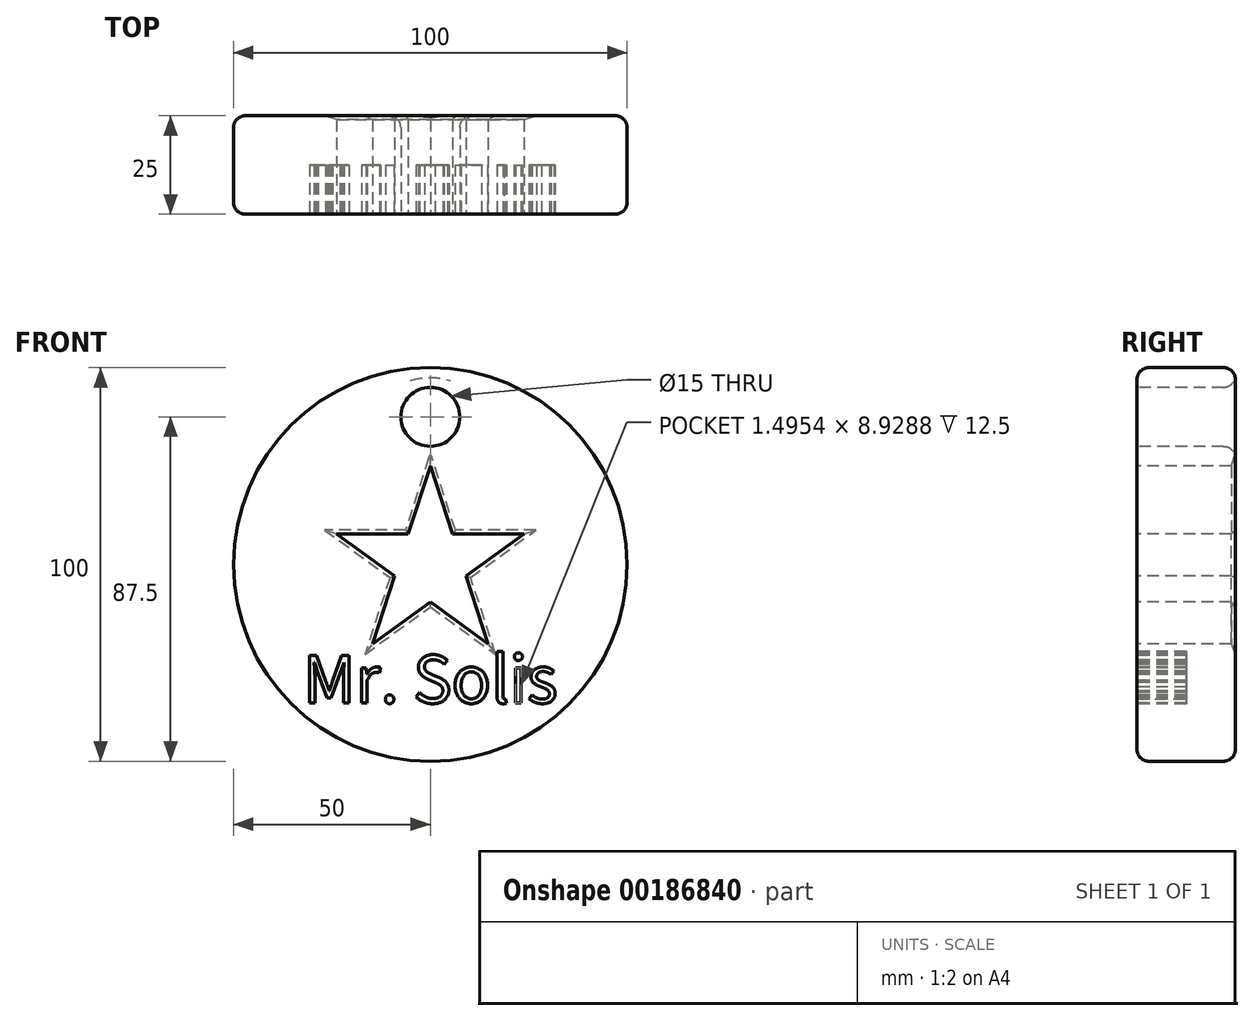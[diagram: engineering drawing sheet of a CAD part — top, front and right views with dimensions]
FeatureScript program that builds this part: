
annotation { "Feature Type Name" : "Feature", "Feature Type Description" : "" }
export const myFeature = defineFeature(function(context is Context, id is Id, definition is map)
    precondition{}
    {
        {
            var Q0;
            Q0=qCreatedBy(makeId("Front.planeOp"),FACE);
            var sketch = newSketch(context, id + "F0", { "sketchPlane" : qUnion([Q0])});
            skCircle(sketch, "E0", {"center": v(0, 0) * mm, "radius": 50 * mm});
            skSolve(sketch);
        }
        {
            var Q0;
            Q0 = qSketchRegion(id + "F0", true);
            extrude(context, id + "F1", {"entities" : qUnion([Q0]), "depth" : 12.5 * mm, "hasSecondDirection" : true, "secondDirectionOppositeDirection" : true, "secondDirectionDepth" : 12.5 * mm});
        }
        {
            var Q0;
            Q0=makeQuery(id+"F1.opExtrude","CAP_FACE",FACE,{"disambiguationData":[OSD([sQuery(id+"F0.wireOp",EDGE,"E0")])],"isStart":false});
            var sketch = newSketch(context, id + "F2", { "sketchPlane" : qUnion([Q0])});
            skCircle(sketch, "E1", {"center": v(0, 37.5) * mm, "radius": 7.5 * mm});
            skSolve(sketch);
        }
        {
            var Q0;
            Q0 = qSketchRegion(id + "F2", true);
            var Q1;
            Q1=makeQuery(id+"F2.imprint","IMPRINT",FACE,{"disambiguationData":[TD([[makeQuery(id+"F2.imprint","IMPRINT",EDGE,{"derivedFrom":sQuery(id+"F2.wireOp",EDGE,"E1")}),1.0]])]});
            extrude(context, id + "F3", {"entities" : qUnion([Q0, Q1]), "operationType" : NewBodyOperationType.REMOVE, "oppositeDirection" : true, "depth" : 26 * mm});
        }
        {
            var Q0;
            Q0=makeQuery(id+"F1.opExtrude","CAP_FACE",FACE,{"disambiguationData":[OSD([sQuery(id+"F0.wireOp",EDGE,"E0")])],"isStart":false});
            var sketch = newSketch(context, id + "F4", { "sketchPlane" : qUnion([Q0])});
            skArc(sketch, "E2.cCircle", {"start": v(1.57, 20.16) * mm, "mid": v(0, 20.23) * mm, "end": v(-1.57, 20.16) * mm, "construction": true});
            skLineSegment(sketch, "E2.0", {"start": v(23.78, 7.73) * mm, "end": v(14.7, -20.23) * mm});
            skLineSegment(sketch, "E2.1", {"start": v(14.7, -20.23) * mm, "end": v(-14.7, -20.23) * mm});
            skLineSegment(sketch, "E2.2", {"start": v(-14.7, -20.23) * mm, "end": v(-23.78, 7.73) * mm});
            skLineSegment(sketch, "E2.3", {"start": v(-23.78, 7.73) * mm, "end": v(0, 25) * mm});
            skLineSegment(sketch, "E2.4", {"start": v(0, 25) * mm, "end": v(23.78, 7.73) * mm});
            skPoint(sketch, "E2.0.midPoint", {"position": v(19.24, -6.25) * mm});
            skLineSegment(sketch, "E3", {"start": v(0, 25) * mm, "end": v(-5.61, 7.73) * mm});
            skLineSegment(sketch, "E4", {"start": v(-23.78, 7.73) * mm, "end": v(-5.61, 7.73) * mm});
            skLineSegment(sketch, "E5", {"start": v(0, 25) * mm, "end": v(5.61, 7.73) * mm});
            skLineSegment(sketch, "E6", {"start": v(-14.7, -20.23) * mm, "end": v(0, -9.55) * mm});
            skLineSegment(sketch, "E7", {"start": v(-23.78, 7.73) * mm, "end": v(-9.08, -2.95) * mm});
            skLineSegment(sketch, "E8.trimOffspring", {"start": v(5.61, 7.73) * mm, "end": v(23.78, 7.73) * mm});
            skLineSegment(sketch, "E9.trimOffspring", {"start": v(-9.08, -2.95) * mm, "end": v(-14.7, -20.23) * mm});
            skLineSegment(sketch, "E10.trimOffspring", {"start": v(9.08, -2.95) * mm, "end": v(14.7, -20.23) * mm});
            skLineSegment(sketch, "E11.trimOffspring", {"start": v(9.08, -2.95) * mm, "end": v(23.78, 7.73) * mm});
            skLineSegment(sketch, "E12.trimOffspring", {"start": v(0, -9.55) * mm, "end": v(14.7, -20.23) * mm});
            skArc(sketch, "E13.trimOffspring", {"start": v(19.66, 4.74) * mm, "mid": v(19.24, 6.25) * mm, "end": v(18.7, 7.73) * mm, "construction": true});
            skArc(sketch, "E14.trimOffspring", {"start": v(10.58, -17.24) * mm, "mid": v(11.89, -16.36) * mm, "end": v(13.12, -15.39) * mm, "construction": true});
            skArc(sketch, "E15.trimOffspring", {"start": v(-13.12, -15.39) * mm, "mid": v(-11.89, -16.36) * mm, "end": v(-10.58, -17.24) * mm, "construction": true});
            skArc(sketch, "E16.trimOffspring", {"start": v(-18.7, 7.73) * mm, "mid": v(-19.24, 6.25) * mm, "end": v(-19.66, 4.74) * mm, "construction": true});
            skSolve(sketch);
        }
        {
            var Q0;
            Q0=makeQuery(id+"F4.imprint","IMPRINT",FACE,{"disambiguationData":[TD([[makeQuery(id+"F4.imprint","IMPRINT",EDGE,{"derivedFrom":sQuery(id+"F4.wireOp",EDGE,"E3")}),1.0]])]});
            extrude(context, id + "F5", {"entities" : qUnion([Q0]), "operationType" : NewBodyOperationType.REMOVE, "oppositeDirection" : true, "depth" : 26 * mm});
        }
        {
            var Q0;
            Q0=makeQuery(id+"F1.opExtrude","CAP_FACE",FACE,{"disambiguationData":[OSD([sQuery(id+"F0.wireOp",EDGE,"E0")])],"isStart":false});
            var sketch = newSketch(context, id + "F6", { "sketchPlane" : qUnion([Q0])});
            skText(sketch, "E17", { "text": "Mr. Solis", "fontName": "NotoSansCJKkr-Regular.otf"});
            const initialGuessF6  = {"E17": [-0.03237, -0.03519, 1, 0, 0.01184]};
            skSetInitialGuess(sketch, initialGuessF6);
            skSolve(sketch);
        }
        {
            var Q0;
            Q0 = qSketchRegion(id + "F6", true);
            extrude(context, id + "F7", {"entities" : qUnion([Q0]), "operationType" : NewBodyOperationType.REMOVE, "oppositeDirection" : true, "depth" : 12.5 * mm});
        }
        {
            var Q0;
            Q0=makeQuery(id+"F5.boolean.opBoolean","COPY",EDGE,{"derivedFrom":makeQuery(id+"F5.opExtrude","CAP_EDGE",EDGE,{"disambiguationData":[OSD([sQuery(id+"F4.wireOp",EDGE,"E3")])],"isStart":true})});
            var Q1;
            Q1=makeQuery(id+"F5.boolean.opBoolean","COPY",EDGE,{"derivedFrom":makeQuery(id+"F5.opExtrude","CAP_EDGE",EDGE,{"disambiguationData":[OSD([sQuery(id+"F4.wireOp",EDGE,"E5")])],"isStart":true})});
            var Q2;
            Q2=makeQuery(id+"F5.boolean.opBoolean","COPY",EDGE,{"derivedFrom":makeQuery(id+"F5.opExtrude","CAP_EDGE",EDGE,{"disambiguationData":[OSD([sQuery(id+"F4.wireOp",EDGE,"E8.trimOffspring")])],"isStart":true})});
            var Q3;
            Q3=makeQuery(id+"F5.boolean.opBoolean","COPY",EDGE,{"derivedFrom":makeQuery(id+"F5.opExtrude","CAP_EDGE",EDGE,{"disambiguationData":[OSD([sQuery(id+"F4.wireOp",EDGE,"E11.trimOffspring")])],"isStart":true})});
            var Q4;
            Q4=makeQuery(id+"F5.boolean.opBoolean","COPY",EDGE,{"derivedFrom":makeQuery(id+"F5.opExtrude","CAP_EDGE",EDGE,{"disambiguationData":[OSD([sQuery(id+"F4.wireOp",EDGE,"E10.trimOffspring")])],"isStart":true})});
            var Q5;
            Q5=makeQuery(id+"F5.boolean.opBoolean","COPY",EDGE,{"derivedFrom":makeQuery(id+"F5.opExtrude","CAP_EDGE",EDGE,{"disambiguationData":[OSD([sQuery(id+"F4.wireOp",EDGE,"E12.trimOffspring")])],"isStart":true})});
            var Q6;
            Q6=makeQuery(id+"F5.boolean.opBoolean","COPY",EDGE,{"derivedFrom":makeQuery(id+"F5.opExtrude","CAP_EDGE",EDGE,{"disambiguationData":[OSD([sQuery(id+"F4.wireOp",EDGE,"E6")])],"isStart":true})});
            var Q7;
            Q7=makeQuery(id+"F5.boolean.opBoolean","COPY",EDGE,{"derivedFrom":makeQuery(id+"F5.opExtrude","CAP_EDGE",EDGE,{"disambiguationData":[OSD([sQuery(id+"F4.wireOp",EDGE,"E9.trimOffspring")])],"isStart":true})});
            var Q8;
            Q8=makeQuery(id+"F5.boolean.opBoolean","COPY",EDGE,{"derivedFrom":makeQuery(id+"F5.opExtrude","CAP_EDGE",EDGE,{"disambiguationData":[OSD([sQuery(id+"F4.wireOp",EDGE,"E7")])],"isStart":true})});
            var Q9;
            Q9=makeQuery(id+"F5.boolean.opBoolean","COPY",EDGE,{"derivedFrom":makeQuery(id+"F5.opExtrude","CAP_EDGE",EDGE,{"disambiguationData":[OSD([sQuery(id+"F4.wireOp",EDGE,"E4")])],"isStart":true})});
            var Q10;
            Q10=makeQuery(id+"F5.boolean.opBoolean","INTERSECT",EDGE,{"derivedFrom":[makeQuery(id+"F1.opExtrude","CAP_FACE",FACE,{"disambiguationData":[OSD([sQuery(id+"F0.wireOp",EDGE,"E0")])],"isStart":true}),makeQuery(id+"F5.opExtrude","SWEPT_FACE",FACE,{"disambiguationData":[OSD([sQuery(id+"F4.wireOp",EDGE,"E5")])]})]});
            var Q11;
            Q11=makeQuery(id+"F5.boolean.opBoolean","INTERSECT",EDGE,{"derivedFrom":[makeQuery(id+"F1.opExtrude","CAP_FACE",FACE,{"disambiguationData":[OSD([sQuery(id+"F0.wireOp",EDGE,"E0")])],"isStart":true}),makeQuery(id+"F5.opExtrude","SWEPT_FACE",FACE,{"disambiguationData":[OSD([sQuery(id+"F4.wireOp",EDGE,"E8.trimOffspring")])]})]});
            var Q12;
            Q12=makeQuery(id+"F5.boolean.opBoolean","INTERSECT",EDGE,{"derivedFrom":[makeQuery(id+"F1.opExtrude","CAP_FACE",FACE,{"disambiguationData":[OSD([sQuery(id+"F0.wireOp",EDGE,"E0")])],"isStart":true}),makeQuery(id+"F5.opExtrude","SWEPT_FACE",FACE,{"disambiguationData":[OSD([sQuery(id+"F4.wireOp",EDGE,"E11.trimOffspring")])]})]});
            var Q13;
            Q13=makeQuery(id+"F5.boolean.opBoolean","INTERSECT",EDGE,{"derivedFrom":[makeQuery(id+"F1.opExtrude","CAP_FACE",FACE,{"disambiguationData":[OSD([sQuery(id+"F0.wireOp",EDGE,"E0")])],"isStart":true}),makeQuery(id+"F5.opExtrude","SWEPT_FACE",FACE,{"disambiguationData":[OSD([sQuery(id+"F4.wireOp",EDGE,"E10.trimOffspring")])]})]});
            var Q14;
            Q14=makeQuery(id+"F5.boolean.opBoolean","INTERSECT",EDGE,{"derivedFrom":[makeQuery(id+"F1.opExtrude","CAP_FACE",FACE,{"disambiguationData":[OSD([sQuery(id+"F0.wireOp",EDGE,"E0")])],"isStart":true}),makeQuery(id+"F5.opExtrude","SWEPT_FACE",FACE,{"disambiguationData":[OSD([sQuery(id+"F4.wireOp",EDGE,"E12.trimOffspring")])]})]});
            var Q15;
            Q15=makeQuery(id+"F5.boolean.opBoolean","INTERSECT",EDGE,{"derivedFrom":[makeQuery(id+"F1.opExtrude","CAP_FACE",FACE,{"disambiguationData":[OSD([sQuery(id+"F0.wireOp",EDGE,"E0")])],"isStart":true}),makeQuery(id+"F5.opExtrude","SWEPT_FACE",FACE,{"disambiguationData":[OSD([sQuery(id+"F4.wireOp",EDGE,"E6")])]})]});
            var Q16;
            Q16=makeQuery(id+"F5.boolean.opBoolean","INTERSECT",EDGE,{"derivedFrom":[makeQuery(id+"F1.opExtrude","CAP_FACE",FACE,{"disambiguationData":[OSD([sQuery(id+"F0.wireOp",EDGE,"E0")])],"isStart":true}),makeQuery(id+"F5.opExtrude","SWEPT_FACE",FACE,{"disambiguationData":[OSD([sQuery(id+"F4.wireOp",EDGE,"E9.trimOffspring")])]})]});
            var Q17;
            Q17=makeQuery(id+"F5.boolean.opBoolean","INTERSECT",EDGE,{"derivedFrom":[makeQuery(id+"F1.opExtrude","CAP_FACE",FACE,{"disambiguationData":[OSD([sQuery(id+"F0.wireOp",EDGE,"E0")])],"isStart":true}),makeQuery(id+"F5.opExtrude","SWEPT_FACE",FACE,{"disambiguationData":[OSD([sQuery(id+"F4.wireOp",EDGE,"E7")])]})]});
            var Q18;
            Q18=makeQuery(id+"F5.boolean.opBoolean","INTERSECT",EDGE,{"derivedFrom":[makeQuery(id+"F1.opExtrude","CAP_FACE",FACE,{"disambiguationData":[OSD([sQuery(id+"F0.wireOp",EDGE,"E0")])],"isStart":true}),makeQuery(id+"F5.opExtrude","SWEPT_FACE",FACE,{"disambiguationData":[OSD([sQuery(id+"F4.wireOp",EDGE,"E4")])]})]});
            var Q19;
            Q19=makeQuery(id+"F5.boolean.opBoolean","INTERSECT",EDGE,{"derivedFrom":[makeQuery(id+"F1.opExtrude","CAP_FACE",FACE,{"disambiguationData":[OSD([sQuery(id+"F0.wireOp",EDGE,"E0")])],"isStart":true}),makeQuery(id+"F5.opExtrude","SWEPT_FACE",FACE,{"disambiguationData":[OSD([sQuery(id+"F4.wireOp",EDGE,"E3")])]})]});
            chamfer(context, id + "F8", {"entities" : qUnion([Q0, Q1, Q2, Q3, Q4, Q5, Q6, Q7, Q8, Q9, Q10, Q11, Q12, Q13, Q14, Q15, Q16, Q17, Q18, Q19]), "width" : 1 * mm, "tangentPropagation" : true});
        }
        {
            var Q0;
            Q0=makeQuery(id+"F1.opExtrude","CAP_EDGE",EDGE,{"disambiguationData":[OSD([sQuery(id+"F0.wireOp",EDGE,"E0")])],"isStart":false});
            var Q1;
            Q1=makeQuery(id+"F1.opExtrude","CAP_EDGE",EDGE,{"disambiguationData":[OSD([sQuery(id+"F0.wireOp",EDGE,"E0")])],"isStart":true});
            var Q2;
            Q2=makeQuery(id+"F3.boolean.opBoolean","INTERSECT",EDGE,{"derivedFrom":[makeQuery(id+"F1.opExtrude","CAP_FACE",FACE,{"disambiguationData":[OSD([sQuery(id+"F0.wireOp",EDGE,"E0")])],"isStart":true}),makeQuery(id+"F3.opExtrude","SWEPT_FACE",FACE,{"disambiguationData":[OSD([sQuery(id+"F2.wireOp",EDGE,"E1")])]})]});
            var Q3;
            Q3=makeQuery(id+"F3.boolean.opBoolean","COPY",EDGE,{"derivedFrom":makeQuery(id+"F3.opExtrude","CAP_EDGE",EDGE,{"disambiguationData":[OSD([sQuery(id+"F2.wireOp",EDGE,"E1")])],"isStart":true})});
            fillet(context, id + "F9", {"entities" : qUnion([Q0, Q1, Q2, Q3]), "radius" : 3 * mm, "tangentPropagation" : true, "allowEdgeOverflow" : false});
        }
    });
